# Revit family: TY-FRB-TY2231_Metric
name_source: partatom
category: Sprinklers
revit_build: Autodesk Revit 2016 (Build: 20150220_1215(x64)
units: mm (PartAtom-declared; Revit-internal decimal feet)

## family parameters
Always vertical = Yes
Cut with Voids When Loaded = No
Maintain Annotation Orientation = No
OmniClass Number = 23.65.70.17.11.24
OmniClass Title = Fire Fighting Sprinkler Heads
Part Type = Normal
Room Calculation Point = No
Round Connector Dimension = Use Diameter
Shared = No
Work Plane-Based = No

## types (17) — shared parameters
COBie = Yes
COBie.Component.Name = Sprinklers:Pendent_SIN
COBie.Type = Yes
COBie.Type.AssetType = Fixed
COBie.Type.Category = Pr_70_55_97_84:Sprinklers
COBie.Type.DurationUnit = year
COBie.Type.Manufacturer = Tyco Fire Protection Products
COBie.Type.Material = Bronze
COBie.Type.Shape = Cylinder
COBie.Type.Size = 1/2"(DN15)
COBie.Type.WarrantyGuarantorParts = http://tycofsbp.com
Coverage = Standard
Coverage_ = Standard
K-Factor = 59.9322
Manufacturer = Tyco Fire Protection Products
Manufacturer URL = www.tyco-fire.com
Material_ = Bronze
Model = TY-FRB
Nominal Diameter 1 = 15 mm
Orifice = Standard
Orifice Size = 10 mm
Outside Diameter 1 = 21 mm
Response = Quick
Response_ = Quick
SIN No = TY2231
Takeout 1 = 56 mm
Technical Data Sheet No = TFP171
zero-valued in all types: COBie.Type.NominalHeight, COBie.Type.NominalLength, COBie.Type.NominalWidth, COBie.Type.ReplacementCost, Style Id

## per-type parameters (varying)
| type | COBie.Component.Description | COBie.Type.Colour | COBie.Type.Finish | COBie.Type.ModelNumber | COBie.Type.ModelReference | Description | Finish_ | Part No | Temperature Rating |
| Pendent Brass 135°F/57°C 4.2K ½" NPT_57-341-1-135 | TY-FRB Wet Pendent  57.2°C K60 DN15 NPT Br | Yellow | Natural Brass | 57-341-1-135 | TY-FRB Wet Pendent  57.2°C K60 DN15 NPT Br | TY-FRB Pendent Brass 135°F/57°C 4.2K ½" NPT | Natural Brass | 57-341-1-135 | 57 °C |
| Pendent Brass 155°F/68°C 4.2K ½" NPT_57-341-1-155 | TY-FRB Wet Pendent  68.3°C K60 DN15 NPT Br | Yellow | Natural Brass | 57-341-1-155 | TY-FRB Wet Pendent  68.3°C K60 DN15 NPT Br | TY-FRB Pendent Brass 155°F/68°C 4.2K ½" NPT | Natural Brass | 57-341-1-155 | 68 °C |
| Pendent Brass 175°F/79°C 4.2K ½" NPT_57-341-1-175 | TY-FRB Wet Pendent  79.4°C K60 DN15 NPT Br | Yellow | Natural Brass | 57-341-1-175 | TY-FRB Wet Pendent  79.4°C K60 DN15 NPT Br | TY-FRB Pendent Brass 175°F/79°C 4.2K ½" NPT | Natural Brass | 57-341-1-175 | 79 °C |
| Pendent Brass 200°F/93°C 4.2K ½" NPT_57-341-1-200 | TY-FRB Wet Pendent  93.3°C K60 DN15 NPT Br | Yellow | Natural Brass | 57-341-1-200 | TY-FRB Wet Pendent  93.3°C K60 DN15 NPT Br | TY-FRB Pendent Brass 200°F/93°C 4.2K ½" NPT | Natural Brass | 57-341-1-200 | 93 °C |
| Pendent Brass 286°F/141°C 4.2K ½" NPT_57-341-1-286 | TY-FRB Wet Pendent  141.1°C K60 DN15 NPT Br | Yellow | Natural Brass | 57-341-1-286 | TY-FRB Wet Pendent  141.1°C K60 DN15 NPT Br | TY-FRB Pendent Brass 286°F/141°C 4.2K ½" NPT | Natural Brass | 57-341-1-286 | 141 °C |
| Pendent White 135°F/57°C 4.2K ½" NPT_57-341-4-135 | TY-FRB Wet Pendent  57.2°C K60 DN15 NPT Wh | White | Signal White | 57-341-4-135 | TY-FRB Wet Pendent  57.2°C K60 DN15 NPT Wh | TY-FRB Pendent White 135°F/57°C 4.2K ½" NPT | White RAL9003 | 57-341-4-135 | 57 °C |
| Pendent White 155°F/68°C 4.2K ½" NPT_57-341-4-155 | TY-FRB Wet Pendent_White_155  68.3°C K60 DN15 NPT Wh | White | Signal White | 57-341-4-155 | TY-FRB Wet Pendent_White_155  68.3°C K60 DN15 NPT Wh | TY-FRB Pendent White 155°F/68°C 4.2K ½" NPT | White RAL9003 | 57-341-4-155 | 68 °C |
| Pendent White 175°F/79°C 4.2K ½" NPT_57-341-4-175 | TY-FRB Wet Pendent  175°F K4.2 1/2 NPT Wh | White | Signal White | 57-341-4-175 | TY-FRB Wet Pendent  175°F K4.2 1/2 NPT Wh | TY-FRB Pendent White 175°F/79°C 4.2K ½" NPT | White RAL9003 | 57-341-4-175 | 79 °C |
| Pendent White 200°F/93°C 4.2K ½" NPT_57-341-4-200 | TY-FRB Wet Pendent  200°F K4.2 1/2 NPT Wh | White | Signal White | 57-341-4-200 | TY-FRB Wet Pendent  200°F K4.2 1/2 NPT Wh | TY-FRB Pendent White 200°F/93°C 4.2K ½" NPT | White RAL9003 | 57-341-4-200 | 93 °C |
| Pendent White 286°F/141°C 4.2K ½" NPT_57-341-4-286 | TY-FRB Wet Pendent  286°F K4.2 1/2 NPT Wh | White | Signal White | 57-341-4-286 | TY-FRB Wet Pendent  286°F K4.2 1/2 NPT Wh | TY-FRB Pendent White 286°F/141°C 4.2K ½" NPT | White RAL9003 | 57-341-4-286 | 141 °C |
| Pendent Jet Black 155°F/68°C 4.2K ½" NPT_57-341-5-155 | TY-FRB Wet Pendent_White_155  155°F K4.2 1/2 NPT Wh | Black | Jet Black | 57-341-5-155 | TY-FRB Wet Pendent_White_155  155°F K4.2 1/2 NPT Wh | TY-FRB Pendent Jet Black 155°F/68°C 4.2K ½" NPT | Jet Black RAL9005 | 57-341-5-155 | 68 °C |
| Pendent Jet Black 155°F/68°C 4.2K ½" NPT_57-341-5-200 | TY-FRB Wet Pendent_Black_155   155°F K4.2 1/2 NPT Wh | Black | Jet Black | 57-341-5-200 | TY-FRB Wet Pendent_Black_155   155°F K4.2 1/2 NPT Wh | TY-FRB Pendent Jet Black 155°F/68°C 4.2K ½" NPT | Jet Black RAL9005 | 57-341-5-200 | 68 °C |
| Pendent Chrome 135°F/57°C 4.2K ½" NPT_57-341-9-135 | TY-FRB Wet Pendent  57.2°C K60 DN15 NPT Chr | Silver | Chrome Plated | 57-341-9-135 | TY-FRB Wet Pendent  57.2°C K60 DN15 NPT Chr | TY-FRB Pendent Chrome 135°F/57°C 4.2K ½" NPT | Chrome Plated | 57-341-9-135 | 57 °C |
| Pendent Chrome 155°F/68°C 4.2K ½" NPT_57-341-9-155 | TY-FRB Wet Pendent  68.3°C K60 DN15 NPT Chr | Silver | Chrome Plated | 57-341-9-155 | TY-FRB Wet Pendent  68.3°C K60 DN15 NPT Chr | TY-FRB Pendent Chrome 155°F/68°C 4.2K ½" NPT | Chrome Plated | 57-341-9-155 | 68 °C |
| Pendent Chrome 175°F/79°C 4.2K ½" NPT_57-341-9-175 | TY-FRB Wet Pendent  79.4°C K60 DN15 NPT Chr | Silver | Chrome Plated | 57-341-9-175 | TY-FRB Wet Pendent  79.4°C K60 DN15 NPT Chr | TY-FRB Pendent Chrome 175°F/79°C 4.2K ½" NPT | Chrome Plated | 57-341-9-175 | 79 °C |
| Pendent Chrome 200°F/93°C 4.2K ½" NPT_57-341-9-200 | TY-FRB Wet Pendent  93.3°C K60 DN15 NPT Chr | Silver | Chrome Plated | 57-341-9-200 | TY-FRB Wet Pendent  93.3°C K60 DN15 NPT Chr | TY-FRB Pendent Chrome 200°F/93°C 4.2K ½" NPT | Chrome Plated | 57-341-9-200 | 93 °C |
| Pendent Chrome 286°F/141°C 4.2K ½" NPT_57-341-9-286 | TY-FRB Wet Pendent  286°F K4.2 1/2 NPT Chr | Silver | Chrome Plated | 57-341-9-286 | TY-FRB Wet Pendent  286°F K4.2 1/2 NPT Chr | TY-FRB Pendent Chrome 286°F/141°C 4.2K ½" NPT | Chrome Plated | 57-341-9-286 | 141 °C |

## geometry (parser evidence)
native form markers: Blend x2, Sweep x49
no freeform markers — native parametric forms only
